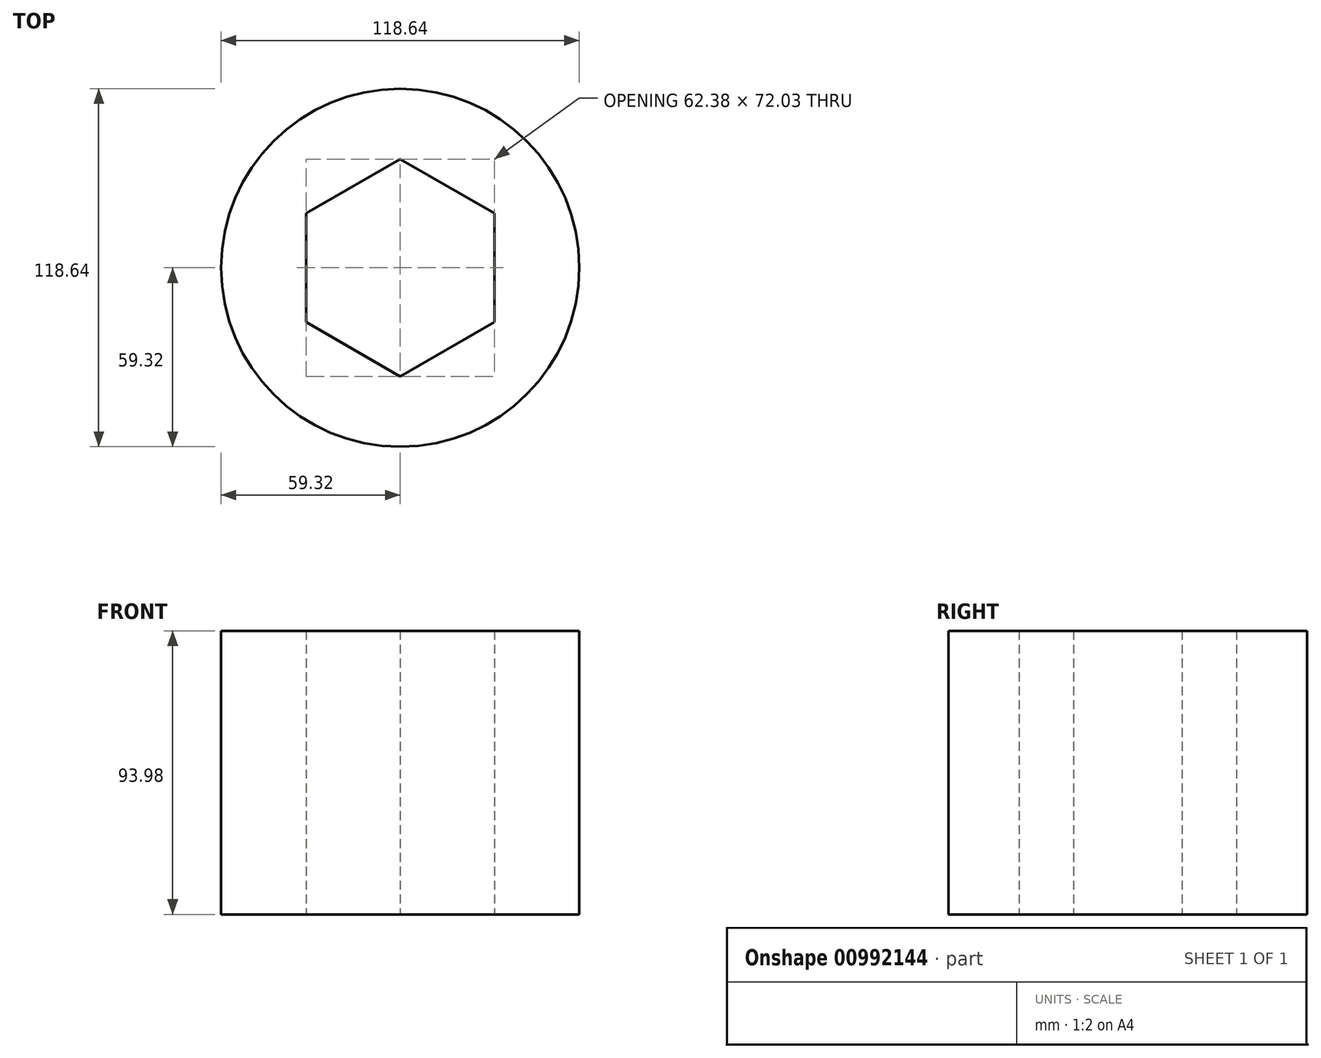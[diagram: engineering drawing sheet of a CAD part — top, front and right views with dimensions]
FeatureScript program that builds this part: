
annotation { "Feature Type Name" : "Feature", "Feature Type Description" : "" }
export const myFeature = defineFeature(function(context is Context, id is Id, definition is map)
    precondition{}
    {
        {
            var Q0;
            Q0=qCreatedBy(makeId("Top.planeOp"),FACE);
            var sketch = newSketch(context, id + "F0", { "sketchPlane" : qUnion([Q0])});
            skCircle(sketch, "E0", {"center": v(0, 0) * mm, "radius": 59.32 * mm});
            skCircle(sketch, "E1.cCircle", {"center": v(0, 0) * mm, "radius": 31.19 * mm, "construction": true});
            skLineSegment(sketch, "E1.0", {"start": v(-31.19, -18) * mm, "end": v(-31.19, 18) * mm});
            skLineSegment(sketch, "E1.1", {"start": v(-31.19, 18) * mm, "end": v(0, 36.01) * mm});
            skLineSegment(sketch, "E1.2", {"start": v(0, 36.01) * mm, "end": v(31.19, 18) * mm});
            skLineSegment(sketch, "E1.3", {"start": v(31.19, 18) * mm, "end": v(31.19, -18) * mm});
            skLineSegment(sketch, "E1.4", {"start": v(31.19, -18) * mm, "end": v(0, -36.01) * mm});
            skLineSegment(sketch, "E1.5", {"start": v(0, -36.01) * mm, "end": v(-31.19, -18) * mm});
            skPoint(sketch, "E1.0.midPoint", {"position": v(-31.19, 0) * mm});
            skSolve(sketch);
        }
        {
            var Q0;
            Q0 = qSketchRegion(id + "F0", true);
            extrude(context, id + "F1", {"entities" : qUnion([Q0]), "depth" : 93.98 * mm, "offsetDistance" : 25.4 * mm});
        }
        {
            var Q0;
            Q0 = qSketchRegion(id + "F0", true);
            extrude(context, id + "F2", {"entities" : qUnion([Q0]), "operationType" : NewBodyOperationType.ADD, "depth" : 25.4 * mm, "offsetDistance" : 25.4 * mm});
        }
    });
